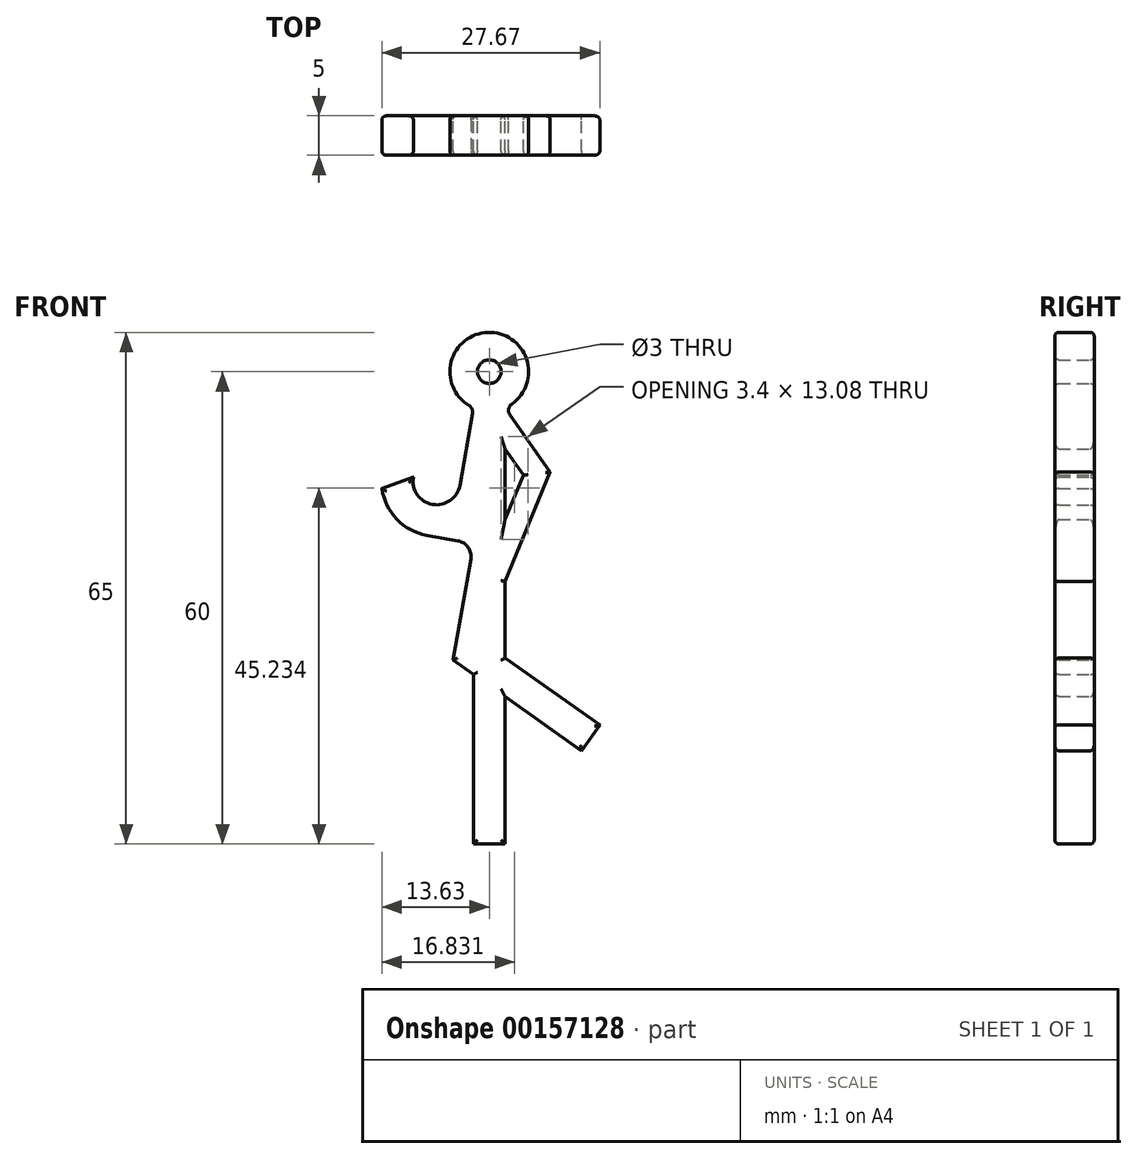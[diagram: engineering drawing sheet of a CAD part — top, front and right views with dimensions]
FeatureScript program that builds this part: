
annotation { "Feature Type Name" : "Feature", "Feature Type Description" : "" }
export const myFeature = defineFeature(function(context is Context, id is Id, definition is map)
    precondition{}
    {
        {
            var Q0;
            Q0=qCreatedBy(makeId("Front.planeOp"),FACE);
            var sketch = newSketch(context, id + "F0", { "sketchPlane" : qUnion([Q0])});
            skCircle(sketch, "E0", {"center": v(0, 0) * mm, "radius": 5 * mm});
            skLineSegment(sketch, "E1", {"start": v(-2, -4.58) * mm, "end": v(-2, -60) * mm});
            skLineSegment(sketch, "E2", {"start": v(-2, -60) * mm, "end": v(2, -60) * mm});
            skLineSegment(sketch, "E3", {"start": v(2, -60) * mm, "end": v(2, -4.58) * mm});
            skLineSegment(sketch, "E4", {"start": v(-2, -4.58) * mm, "end": v(-3.74, -14.43) * mm});
            skArc(sketch, "E5", {"start": v(-9.65, -13.39) * mm, "mid": v(-7.21, -16.86) * mm, "end": v(-3.74, -14.43) * mm});
            skArc(sketch, "E6.0", {"start": v(-13.63, -14.84) * mm, "mid": v(-11.74, -18.76) * mm, "end": v(-7.9, -20.8) * mm});
            skLineSegment(sketch, "E7", {"start": v(-7.9, -20.8) * mm, "end": v(-2, -21.84) * mm});
            skLineSegment(sketch, "E8", {"start": v(2, -4.58) * mm, "end": v(7.74, -12.77) * mm});
            skLineSegment(sketch, "E9", {"start": v(7.74, -12.77) * mm, "end": v(2, -26.63) * mm});
            skLineSegment(sketch, "E10.0", {"start": v(4.33, -13.15) * mm, "end": v(-0.77, -25.49) * mm});
            skLineSegment(sketch, "E10.1", {"start": v(-0.46, -6.3) * mm, "end": v(4.33, -13.15) * mm});
            skLineSegment(sketch, "E11", {"start": v(-2, -21.84) * mm, "end": v(-4.6, -36.62) * mm});
            skLineSegment(sketch, "E12", {"start": v(-4.6, -36.62) * mm, "end": v(11.73, -48.16) * mm});
            skLineSegment(sketch, "E13.0", {"start": v(-0.23, -34.81) * mm, "end": v(14.04, -44.9) * mm});
            skLineSegment(sketch, "E13.1", {"start": v(1.94, -22.54) * mm, "end": v(-0.23, -34.81) * mm});
            skLineSegment(sketch, "E14", {"start": v(11.73, -48.16) * mm, "end": v(14.04, -44.9) * mm});
            skCircle(sketch, "E15", {"center": v(0, 0) * mm, "radius": 1.5 * mm});
            skLineSegment(sketch, "E16", {"start": v(-9.65, -13.39) * mm, "end": v(-13.63, -14.84) * mm});
            skSolve(sketch);
        }
        {
            var Q0;
            Q0=makeQuery(id+"F0.imprint","IMPRINT",FACE,{"disambiguationData":[TD([[makeQuery(id+"F0.imprint","IMPRINT",EDGE,{"derivedFrom":sQuery(id+"F0.wireOp",EDGE,"E15")}),-1.0]])]});
            var Q1;
            {var subQ0=sQuery(id+"F0.wireOp",EDGE,"E4");Q1=makeQuery(id+"F0.imprint","IMPRINT",FACE,{"disambiguationData":[TD([[makeQuery(id+"F0.imprint","IMPRINT",EDGE,{"derivedFrom":subQ0}),1.0]])]});}
            var Q2;
            {var subQ0=sQuery(id+"F0.wireOp",EDGE,"E3");var subQ1=makeQuery(id+"F0.imprint","INTERSECT",VERTEX,{"derivedFrom":[subQ0,sQuery(id+"F0.wireOp",EDGE,"E13.0")]});Q2=makeQuery(id+"F0.imprint","IMPRINT",FACE,{"disambiguationData":[TD([[makeQuery(id+"F0.imprint","IMPRINT",EDGE,{"disambiguationData":[TD([[subQ1,1.0]])],"derivedFrom":subQ0}),1.0]])]});}
            var Q3;
            {var subQ1=sQuery(id+"F0.wireOp",EDGE,"E8");Q3=makeQuery(id+"F0.imprint","IMPRINT",FACE,{"disambiguationData":[TD([[makeQuery(id+"F0.imprint","IMPRINT",EDGE,{"derivedFrom":subQ1}),-1.0]])]});}
            var Q4;
            {var subQ0=sQuery(id+"F0.wireOp",EDGE,"E11");Q4=makeQuery(id+"F0.imprint","IMPRINT",FACE,{"disambiguationData":[TD([[makeQuery(id+"F0.imprint","IMPRINT",EDGE,{"derivedFrom":subQ0}),1.0]])]});}
            var Q5;
            {var subQ5=sQuery(id+"F0.wireOp",EDGE,"E14");Q5=makeQuery(id+"F0.imprint","IMPRINT",FACE,{"disambiguationData":[TD([[makeQuery(id+"F0.imprint","IMPRINT",EDGE,{"derivedFrom":subQ5}),1.0]])]});}
            var Q6;
            {var subQ0=sQuery(id+"F0.wireOp",EDGE,"E2");Q6=makeQuery(id+"F0.imprint","IMPRINT",FACE,{"disambiguationData":[TD([[makeQuery(id+"F0.imprint","IMPRINT",EDGE,{"derivedFrom":subQ0}),1.0]])]});}
            extrude(context, id + "F1", {"entities" : qUnion([Q0, Q1, Q2, Q3, Q4, Q5, Q6]), "depth" : 5 * mm});
        }
        {
            var Q0;
            Q0=makeQuery(id+"F1.opExtrude","SWEPT_EDGE",EDGE,{"disambiguationData":[OSD([sQuery(id+"F0.wireOp",EDGE,"E1"),sQuery(id+"F0.wireOp",EDGE,"E7"),sQuery(id+"F0.wireOp",EDGE,"E11")])]});
            fillet(context, id + "F2", {"entities" : qUnion([Q0]), "radius" : 2 * mm, "tangentPropagation" : true, "allowEdgeOverflow" : false});
        }
        {
            var Q0;
            Q0=makeQuery(id+"F1.opExtrude","SWEPT_EDGE",EDGE,{"disambiguationData":[OSD([sQuery(id+"F0.wireOp",EDGE,"E0"),sQuery(id+"F0.wireOp",EDGE,"E1"),sQuery(id+"F0.wireOp",EDGE,"E4")])]});
            var Q1;
            Q1=makeQuery(id+"F1.opExtrude","SWEPT_EDGE",EDGE,{"disambiguationData":[OSD([sQuery(id+"F0.wireOp",EDGE,"E0"),sQuery(id+"F0.wireOp",EDGE,"E3"),sQuery(id+"F0.wireOp",EDGE,"E8")])]});
            fillet(context, id + "F3", {"entities" : qUnion([Q0, Q1]), "radius" : 1 * mm, "tangentPropagation" : true, "allowEdgeOverflow" : false});
        }
        {
            var Q0;
            Q0=makeQuery(id+"F1.opExtrude","CAP_FACE",FACE,{"disambiguationData":[OSD([sQuery(id+"F0.wireOp",EDGE,"E0"),sQuery(id+"F0.wireOp",EDGE,"E1"),sQuery(id+"F0.wireOp",EDGE,"E2"),sQuery(id+"F0.wireOp",EDGE,"E3"),sQuery(id+"F0.wireOp",EDGE,"E4"),sQuery(id+"F0.wireOp",EDGE,"WC0twwlv-RLqS-m5eM-BMo5-ymsuJj7iIFNo"),sQuery(id+"F0.wireOp",EDGE,"E5"),sQuery(id+"F0.wireOp",EDGE,"E6.0"),sQuery(id+"F0.wireOp",EDGE,"E7"),sQuery(id+"F0.wireOp",EDGE,"E8"),sQuery(id+"F0.wireOp",EDGE,"E9"),sQuery(id+"F0.wireOp",EDGE,"E10.0"),sQuery(id+"F0.wireOp",EDGE,"E10.1"),sQuery(id+"F0.wireOp",EDGE,"E11"),sQuery(id+"F0.wireOp",EDGE,"E12"),sQuery(id+"F0.wireOp",EDGE,"E13.0"),sQuery(id+"F0.wireOp",EDGE,"E14"),sQuery(id+"F0.wireOp",EDGE,"E15")])],"isStart":false});
            var Q1;
            Q1=makeQuery(id+"F1.opExtrude","CAP_FACE",FACE,{"disambiguationData":[OSD([sQuery(id+"F0.wireOp",EDGE,"E0"),sQuery(id+"F0.wireOp",EDGE,"E1"),sQuery(id+"F0.wireOp",EDGE,"E2"),sQuery(id+"F0.wireOp",EDGE,"E3"),sQuery(id+"F0.wireOp",EDGE,"E4"),sQuery(id+"F0.wireOp",EDGE,"WC0twwlv-RLqS-m5eM-BMo5-ymsuJj7iIFNo"),sQuery(id+"F0.wireOp",EDGE,"E5"),sQuery(id+"F0.wireOp",EDGE,"E6.0"),sQuery(id+"F0.wireOp",EDGE,"E7"),sQuery(id+"F0.wireOp",EDGE,"E8"),sQuery(id+"F0.wireOp",EDGE,"E9"),sQuery(id+"F0.wireOp",EDGE,"E10.0"),sQuery(id+"F0.wireOp",EDGE,"E10.1"),sQuery(id+"F0.wireOp",EDGE,"E11"),sQuery(id+"F0.wireOp",EDGE,"E12"),sQuery(id+"F0.wireOp",EDGE,"E13.0"),sQuery(id+"F0.wireOp",EDGE,"E14"),sQuery(id+"F0.wireOp",EDGE,"E15")])],"isStart":true});
            fillet(context, id + "F4", {"entities" : qUnion([Q0, Q1]), "radius" : 0.5 * mm, "tangentPropagation" : true, "allowEdgeOverflow" : false});
        }
    });
